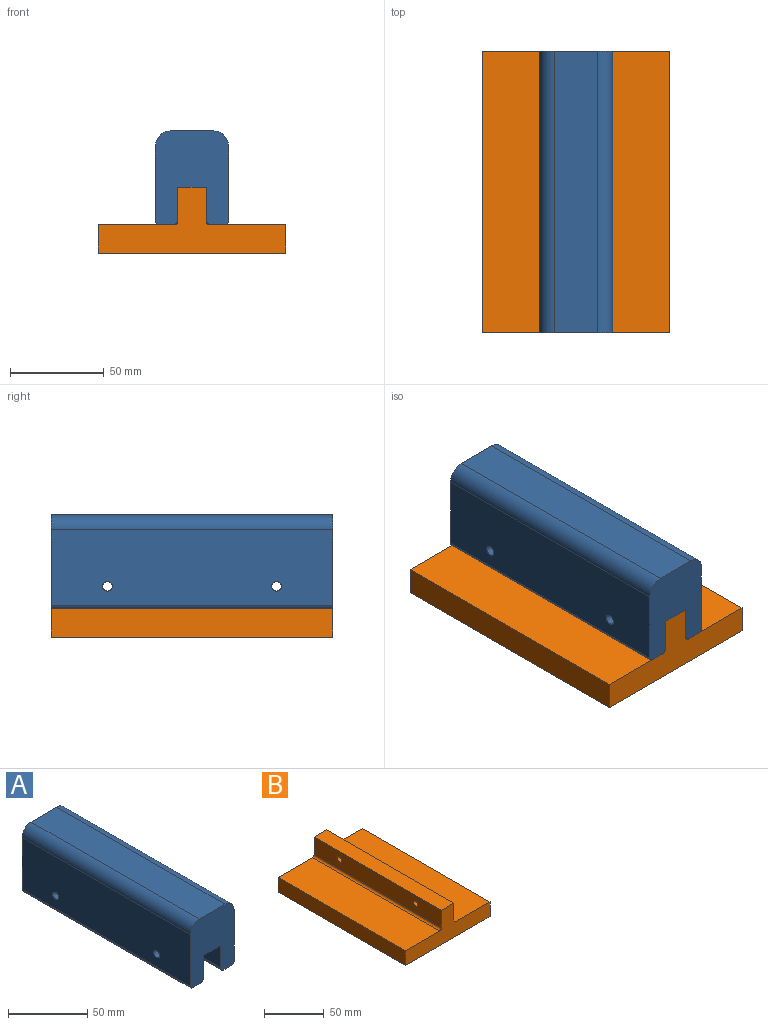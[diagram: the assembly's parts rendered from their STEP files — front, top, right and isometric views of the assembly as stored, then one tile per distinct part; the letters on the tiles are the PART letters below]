
ASSEMBLY  parts=2 mates=1
PART A: 20 faces, bbox 39x150x50 mm
  f0: plane 150x40mm, normal (-1,0,0), area 5957.5mm2, adj f8,f9,f13,f14,f18,f19
  f1: plane 150x7mm, normal (0,0,-1), area 1050mm2, adj f8,f9,f10,f14
  f2: plane 150x17mm, normal (1,0,0), area 2507.5mm2, adj f3,f8,f9,f10,f18,f19
  f3: plane 150x15mm, normal (0,0,-1), area 2250mm2, adj f2,f4,f8,f9
  f4: plane 150x17mm, normal (-1,0,0), area 2507.5mm2, adj f3,f8,f9,f11,f16,f17
  f5: plane 150x7mm, normal (0,0,-1), area 1050mm2, adj f8,f9,f11,f15
  f6: plane 150x40mm, normal (1,0,0), area 5957.5mm2, adj f8,f9,f12,f15,f16,f17
  f7: plane 150x23mm, normal (0,0,1), area 3450mm2, adj f8,f9,f12,f13
  f8: plane 50x39mm, normal (0,-1,0), area 1617mm2, adj f0,f1,f2,f3,f4,f5,f6,f7
  f9: plane 50x39mm, normal (0,1,0), area 1617mm2, adj f0,f1,f2,f3,f4,f5,f6,f7
  f10: cylinder r=3mm len=150mm, axis (0,1,0), area 706.9mm2, adj f1,f2,f8,f9
  f11: cylinder r=3mm len=150mm, axis (0,1,0), area 706.9mm2, adj f4,f5,f8,f9
  f12: cylinder r=8mm len=150mm, axis (0,1,0), area 1885mm2, adj f6,f7,f8,f9
  f13: cylinder r=8mm len=150mm, axis (0,1,0), area 1885mm2, adj f0,f7,f8,f9
  f14: cylinder r=2mm len=150mm, axis (0,1,0), area 471.2mm2, adj f0,f1,f8,f9
  f15: cylinder r=2mm len=150mm, axis (0,1,0), area 471.2mm2, adj f5,f6,f8,f9
  f16: cylinder r=2.6mm len=12mm, axis (-1,0,0), area 196mm2, adj f4,f6
  f17: cylinder r=2.6mm len=12mm, axis (-1,0,0), area 196mm2, adj f4,f6
  f18: cylinder r=2.6mm len=12mm, axis (-1,0,0), area 196mm2, adj f0,f2
  f19: cylinder r=2.6mm len=12mm, axis (-1,0,0), area 196mm2, adj f0,f2
PART B: 14 faces, bbox 100x150x35 mm
  f0: plane 150x15mm, normal (-1,0,0), area 2250mm2, adj f1,f7,f8,f9
  f1: plane 150x100mm, normal (0,0,-1), area 15000mm2, adj f0,f2,f8,f9
  f2: plane 150x15mm, normal (1,0,0), area 2250mm2, adj f1,f3,f8,f9
  f3: plane 150x40.5mm, normal (0,0,1), area 6075mm2, adj f2,f8,f9,f12
  f4: plane 150x18mm, normal (1,0,0), area 2659.1mm2, adj f5,f8,f9,f10,f11,f12
  f5: plane 150x15mm, normal (0,0,1), area 2250mm2, adj f4,f6,f8,f9
  f6: plane 150x18mm, normal (-1,0,0), area 2659.1mm2, adj f5,f8,f9,f10,f11,f13
  f7: plane 150x40.5mm, normal (0,0,1), area 6075mm2, adj f0,f8,f9,f13
  f8: plane 100x35mm, normal (0,-1,0), area 1801.7mm2, adj f0,f1,f2,f3,f4,f5,f6,f7
  f9: plane 100x35mm, normal (0,1,0), area 1801.7mm2, adj f0,f1,f2,f3,f4,f5,f6,f7
  f10: cylinder r=2.55mm len=15mm, axis (1,0,0), area 240.3mm2, adj f4,f6
  f11: cylinder r=2.55mm len=15mm, axis (1,0,0), area 240.3mm2, adj f4,f6
  f12: cylinder r=2mm len=150mm, axis (0,-1,0), area 471.2mm2, adj f3,f4,f8,f9
  f13: cylinder r=2mm len=150mm, axis (0,-1,0), area 471.2mm2, adj f6,f7,f8,f9
PLACE A t=(-63.23,47.9,-25.52)mm
PLACE B t=(-60.8,47.9,-40.52)mm
MATE fastened A.f8 <-> B.f8  axis (0,-1,0) through (-63.97,-102.1,-5.52)mm
